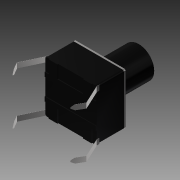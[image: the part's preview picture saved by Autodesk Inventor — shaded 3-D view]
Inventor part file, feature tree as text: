
AUTODESK INVENTOR PART (.ipt)
format: ipt  version: 2014 SP2 (Build 180246200, 246)  size: 308,224 bytes
history: native  units: mm
features: sketch x14, extrude x12, fillet x7, mirror x1, projected_geometry x1
ambient origin geometry x8: Origin, YZ Plane, XZ Plane, XY Plane, X Axis, Y Axis, Z Axis, Center Point
bodies: Solid1 (feature_tree)
feature tree (35):
  extrude  "Extrusion1"  Depth=4.52mm TaperAngle=0.0deg
  extrude  "Extrusion2"  Depth=0.2mm TaperAngle=0.0deg
  extrude  "Extrusion3"  Depth=0.2mm TaperAngle=0.0deg
  extrude  "Extrusion4"  Depth=0.2mm
  extrude  "Extrusion5"  Depth=0.6mm TaperAngle=0.0deg
  fillet  "Fillet1"  Radius=0.6mm
  fillet  "Fillet2"  Radius=0.6mm
  fillet  "Fillet3"  Radius=0.1mm
  extrude  "Extrusion6"  Depth=0.1mm
  mirror  "Mirror1"
  extrude  "Extrusion7"  Depth=0.1mm
  extrude  "Extrusion8"  Depth=0.1mm
  fillet  "Fillet4"  Radius=0.1mm
  sketch  "3D Sketch1"
  sketch  "3D Sketch2"
  extrude  "Extrusion9"  [1 undecoded]
  fillet  "Fillet5"  [1 undecoded]
  extrude  "Extrusion10"  [1 undecoded]
  fillet  "Fillet6"  [1 undecoded]
  extrude  "Extrusion11"  [1 undecoded]
  fillet  "Fillet7"  [1 undecoded]
  extrude  "Extrusion12"  [1 undecoded]
  sketch  "Sketch1"  dims[d3=3.4mm d4=0.0mm d5=4.52mm d6=3.4mm d7=0.0mm d8=0.0mm]
  sketch  "Sketch2"  dims[d11=0.2mm d12=0.0mm d15=0.2mm d16=0.0mm]
  sketch  "Sketch3"  dims[d20=20.0mm d22=4.53mm d23=20.0mm d25=4.53mm d28=0.2mm d29=0.0mm]
  sketch  "Sketch4"  dims[d30=0.2mm d31=0.2mm]
  sketch  "Sketch5"  dims[d32=0.2mm d39=0.6mm d40=0.0mm d43=0.6mm d44=0.0mm d45=0.6mm d46=0.0mm d47=0.1mm]
  projected_geometry  "Projected Loop1"
  sketch  "Sketch6"  dims[d49=0.6mm d50=0.0mm d51=0.1mm]
  sketch  "Sketch7"  dims[d55=0.6mm d56=0.0mm d57=0.1mm]
  sketch  "Sketch8"  dims[d60=0.6mm d61=0.0mm d62=0.1mm d69=0.1mm d70=0.0mm]
  sketch  "Sketch9"
  sketch  "Sketch10"
  sketch  "Sketch11"
  sketch  "Sketch12"
note: 7 required parameter values undecoded (feature->parameter linkage not recoverable at this tier; creation-order binding heuristic only, values carry confidence <= 0.55)
